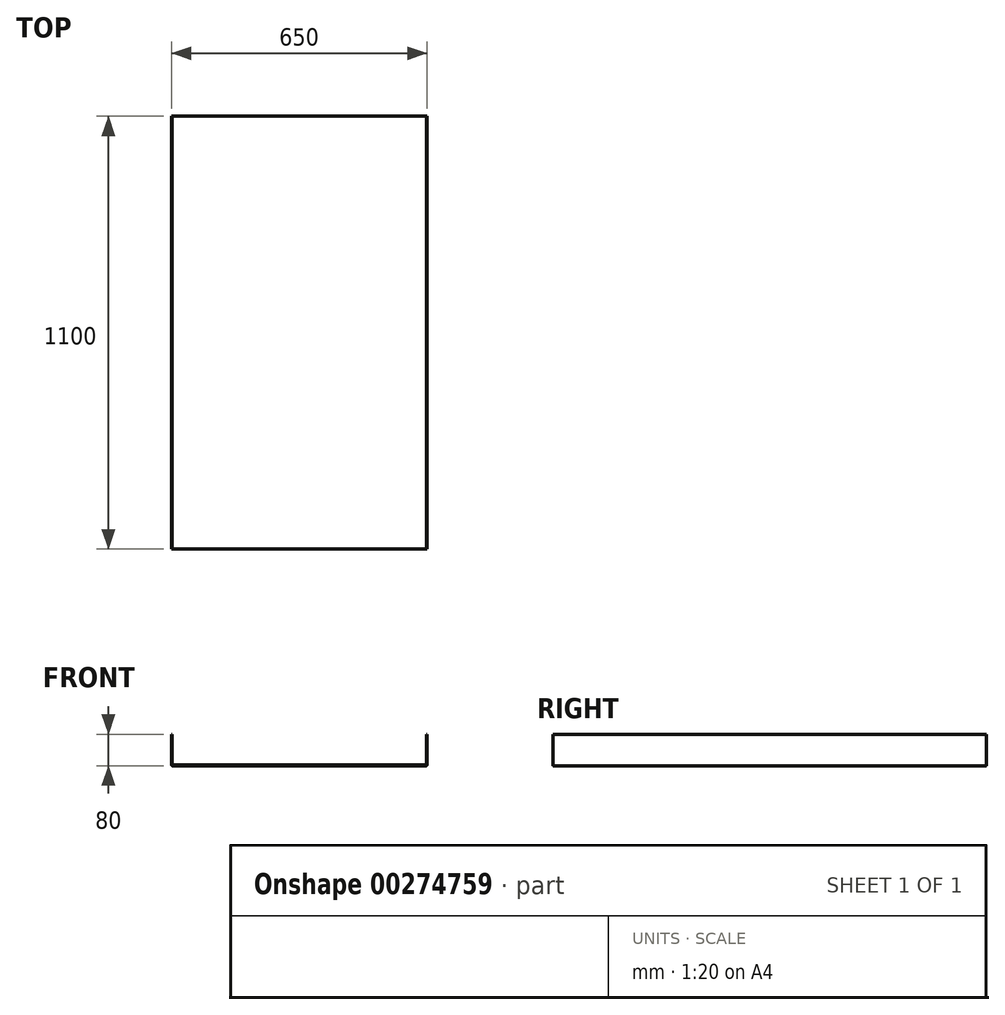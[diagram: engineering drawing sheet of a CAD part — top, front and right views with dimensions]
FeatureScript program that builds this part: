
annotation { "Feature Type Name" : "Feature", "Feature Type Description" : "" }
export const myFeature = defineFeature(function(context is Context, id is Id, definition is map)
    precondition{}
    {
        {
            var Q0;
            Q0=qCreatedBy(makeId("Top.planeOp"),FACE);
            var sketch = newSketch(context, id + "F0", { "sketchPlane" : qUnion([Q0])});
            skLineSegment(sketch, "E0", {"start": v(-308.62, 0) * mm, "end": v(341.38, 0) * mm});
            skLineSegment(sketch, "E1", {"start": v(-308.62, 0) * mm, "end": v(-308.62, 1100) * mm});
            skLineSegment(sketch, "E2", {"start": v(-308.62, 1100) * mm, "end": v(341.38, 1100) * mm});
            skLineSegment(sketch, "E3", {"start": v(341.38, 1100) * mm, "end": v(341.38, 0) * mm});
            skSolve(sketch);
        }
        {
            var Q0;
            Q0=makeQuery(id+"F0.imprint","IMPRINT",FACE,{"disambiguationData":[TD([[makeQuery(id+"F0.imprint","IMPRINT",EDGE,{"derivedFrom":sQuery(id+"F0.wireOp",EDGE,"E0")}),1.0]])]});
            extrude(context, id + "F1", {"entities" : qUnion([Q0]), "depth" : 1.5 * mm});
        }
        {
            var Q0;
            Q0=makeQuery(id+"F1.opExtrude","SWEPT_FACE",FACE,{"disambiguationData":[OSD([sQuery(id+"F0.wireOp",EDGE,"E1")])]});
            var sketch = newSketch(context, id + "F2", { "sketchPlane" : qUnion([Q0])});
            skLineSegment(sketch, "E4.bottom", {"start": v(-1100, 0) * mm, "end": v(0, 0) * mm});
            skLineSegment(sketch, "E4.top", {"start": v(-1100, 80) * mm, "end": v(0, 80) * mm});
            skLineSegment(sketch, "E4.left", {"start": v(-1100, 0) * mm, "end": v(-1100, 80) * mm});
            skLineSegment(sketch, "E4.right", {"start": v(0, 0) * mm, "end": v(0, 80) * mm});
            skSolve(sketch);
        }
        {
            var Q0;
            {var subQ0=sQuery(id+"F2.wireOp",EDGE,"E4.top");Q0=makeQuery(id+"F2.imprint","IMPRINT",FACE,{"disambiguationData":[TD([[makeQuery(id+"F2.imprint","IMPRINT",EDGE,{"derivedFrom":subQ0}),-1.0]])]});}
            extrude(context, id + "F3", {"entities" : qUnion([Q0]), "oppositeDirection" : true, "depth" : 1.5 * mm});
        }
        {
            var Q0;
            Q0=makeQuery(id+"F1.opExtrude","CAP_EDGE",EDGE,{"disambiguationData":[OSD([sQuery(id+"F0.wireOp",EDGE,"E1")])],"isStart":true});
            fillet(context, id + "F4", {"entities" : qUnion([Q0]), "radius" : 2 * mm, "tangentPropagation" : true, "allowEdgeOverflow" : false});
        }
        {
            var Q0;
            Q0=makeQuery(id+"F1.opExtrude","SWEPT_FACE",FACE,{"disambiguationData":[OSD([sQuery(id+"F0.wireOp",EDGE,"E3")])]});
            var sketch = newSketch(context, id + "F5", { "sketchPlane" : qUnion([Q0])});
            skLineSegment(sketch, "E5.bottom", {"start": v(0, 0) * mm, "end": v(1100, 0) * mm});
            skLineSegment(sketch, "E5.top", {"start": v(0, 80) * mm, "end": v(1100, 80) * mm});
            skLineSegment(sketch, "E5.left", {"start": v(0, 0) * mm, "end": v(0, 80) * mm});
            skLineSegment(sketch, "E5.right", {"start": v(1100, 0) * mm, "end": v(1100, 80) * mm});
            skSolve(sketch);
        }
        {
            var Q0;
            {var subQ0=sQuery(id+"F5.wireOp",EDGE,"E5.top");Q0=makeQuery(id+"F5.imprint","IMPRINT",FACE,{"disambiguationData":[TD([[makeQuery(id+"F5.imprint","IMPRINT",EDGE,{"derivedFrom":subQ0}),-1.0]])]});}
            extrude(context, id + "F6", {"entities" : qUnion([Q0]), "operationType" : NewBodyOperationType.ADD, "oppositeDirection" : true, "depth" : 1.5 * mm});
        }
        {
            var Q0;
            Q0=makeQuery(id+"F1.opExtrude","CAP_EDGE",EDGE,{"disambiguationData":[OSD([sQuery(id+"F0.wireOp",EDGE,"E3")])],"isStart":true});
            fillet(context, id + "F7", {"entities" : qUnion([Q0]), "radius" : 2 * mm, "tangentPropagation" : true, "allowEdgeOverflow" : false});
        }
    });
